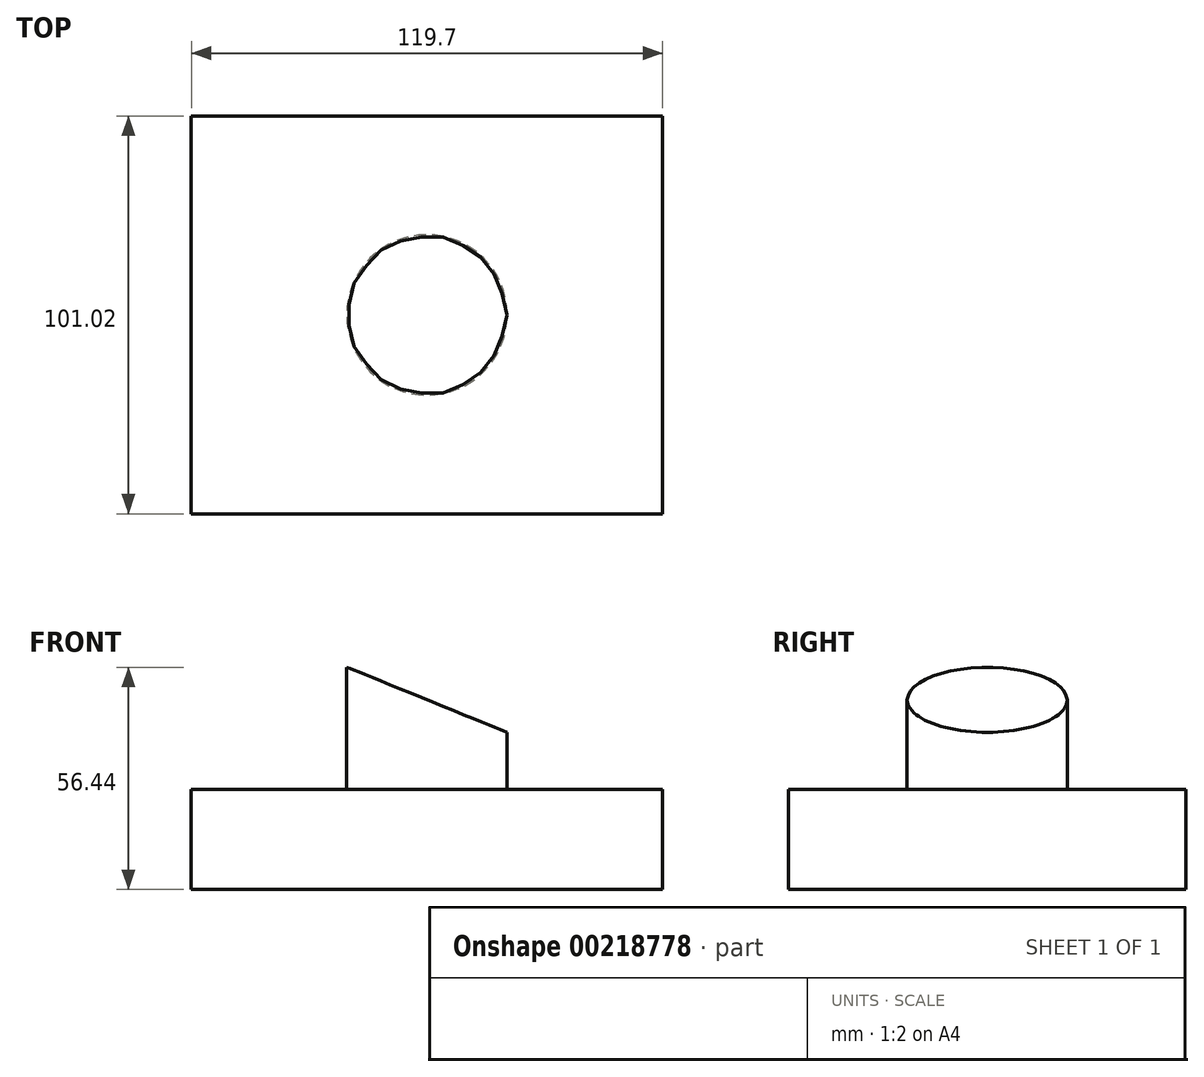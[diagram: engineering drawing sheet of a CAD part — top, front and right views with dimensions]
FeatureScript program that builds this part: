
annotation { "Feature Type Name" : "Feature", "Feature Type Description" : "" }
export const myFeature = defineFeature(function(context is Context, id is Id, definition is map)
    precondition{}
    {
        {
            var Q0;
            Q0=qCreatedBy(makeId("Top.planeOp"),FACE);
            var sketch = newSketch(context, id + "F0", { "sketchPlane" : qUnion([Q0])});
            skLineSegment(sketch, "E0.bottom", {"start": v(59.85, -50.51) * mm, "end": v(-59.85, -50.51) * mm});
            skLineSegment(sketch, "E0.top", {"start": v(59.85, 50.51) * mm, "end": v(-59.85, 50.51) * mm});
            skLineSegment(sketch, "E0.left", {"start": v(59.85, -50.51) * mm, "end": v(59.85, 50.51) * mm});
            skLineSegment(sketch, "E0.right", {"start": v(-59.85, -50.51) * mm, "end": v(-59.85, 50.51) * mm});
            skPoint(sketch, "E0.middle", {"position": v(0, 0) * mm});
            skSolve(sketch);
        }
        {
            var Q0;
            Q0=makeQuery(id+"F0.imprint","IMPRINT",FACE,{"disambiguationData":[TD([[makeQuery(id+"F0.imprint","IMPRINT",EDGE,{"derivedFrom":sQuery(id+"F0.wireOp",EDGE,"E0.bottom")}),-1.0]])]});
            extrude(context, id + "F1", {"entities" : qUnion([Q0]), "depth" : 25.4 * mm});
        }
        {
            var Q0;
            Q0=makeQuery(id+"F1.opExtrude","CAP_FACE",FACE,{"disambiguationData":[OSD([sQuery(id+"F0.wireOp",EDGE,"E0.bottom"),sQuery(id+"F0.wireOp",EDGE,"E0.top"),sQuery(id+"F0.wireOp",EDGE,"E0.left"),sQuery(id+"F0.wireOp",EDGE,"E0.right")])],"isStart":false});
            var sketch = newSketch(context, id + "F2", { "sketchPlane" : qUnion([Q0])});
            skCircle(sketch, "E1", {"center": v(0, 0) * mm, "radius": 20.35 * mm});
            skSolve(sketch);
        }
        {
            var Q0;
            Q0=makeQuery(id+"F2.imprint","IMPRINT",FACE,{"disambiguationData":[TD([[makeQuery(id+"F2.imprint","IMPRINT",EDGE,{"derivedFrom":sQuery(id+"F2.wireOp",EDGE,"E1")}),1.0]])]});
            extrude(context, id + "F3", {"entities" : qUnion([Q0]), "operationType" : NewBodyOperationType.ADD, "depth" : 32 * mm});
        }
        {
            var Q0;
            Q0=qCreatedBy(makeId("Front.planeOp"),FACE);
            var sketch = newSketch(context, id + "F4", { "sketchPlane" : qUnion([Q0])});
            skLineSegment(sketch, "E2", {"start": v(-23, 57.52) * mm, "end": v(24.73, 57.52) * mm});
            skLineSegment(sketch, "E3", {"start": v(24.73, 57.52) * mm, "end": v(24.73, 38.12) * mm});
            skLineSegment(sketch, "E4", {"start": v(24.73, 38.12) * mm, "end": v(-23, 57.52) * mm});
            skSolve(sketch);
        }
        {
            var Q0;
            Q0=makeQuery(id+"F4.imprint","IMPRINT",FACE,{"disambiguationData":[TD([[makeQuery(id+"F4.imprint","IMPRINT",EDGE,{"derivedFrom":sQuery(id+"F4.wireOp",EDGE,"E2")}),-1.0]])]});
            extrude(context, id + "F5", {"entities" : qUnion([Q0]), "operationType" : NewBodyOperationType.REMOVE, "endBound" : BoundingType.SYMMETRIC, "oppositeDirection" : true, "depth" : 127 * mm});
        }
    });
